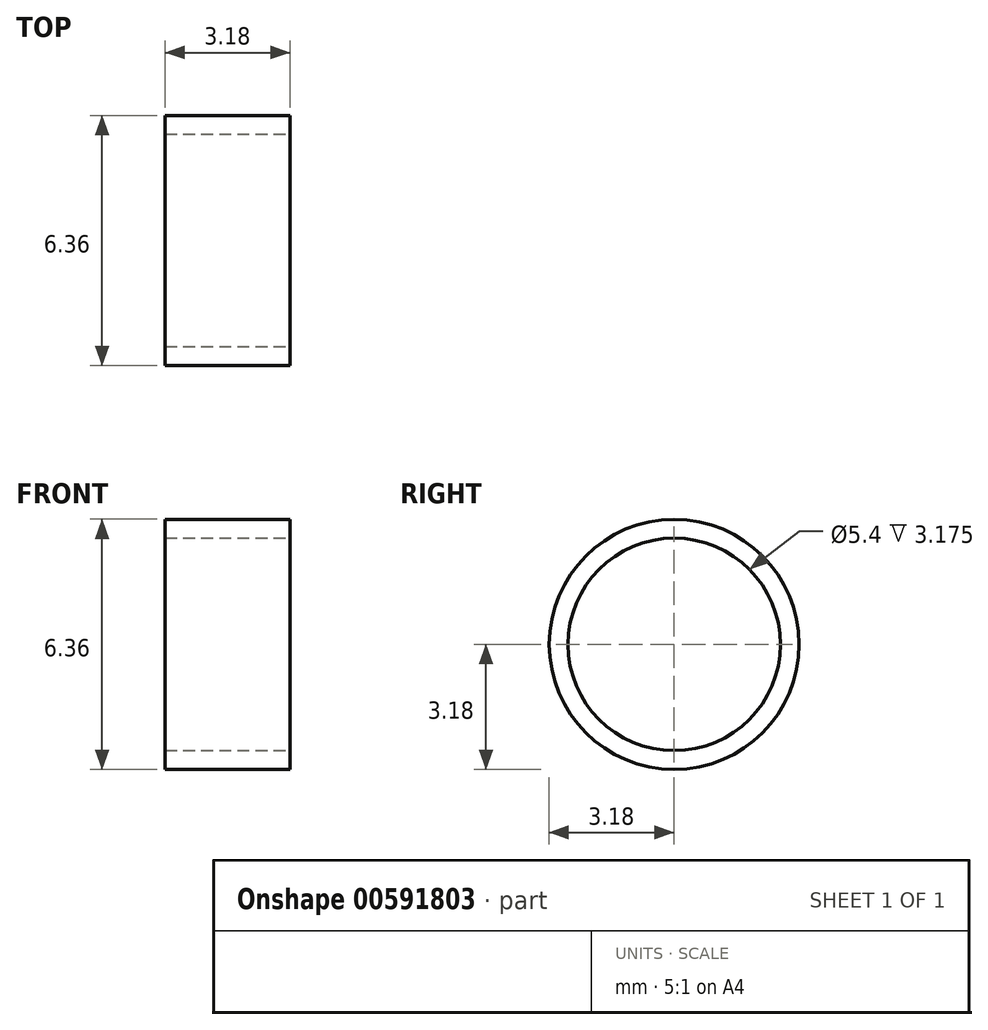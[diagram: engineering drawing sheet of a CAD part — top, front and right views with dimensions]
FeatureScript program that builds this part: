
annotation { "Feature Type Name" : "Feature", "Feature Type Description" : "" }
export const myFeature = defineFeature(function(context is Context, id is Id, definition is map)
    precondition{}
    {
        {
            var Q0;
            Q0=qCreatedBy(makeId("Right.planeOp"),FACE);
            var sketch = newSketch(context, id + "F0", { "sketchPlane" : qUnion([Q0])});
            skCircle(sketch, "E0", {"center": v(0, 0) * mm, "radius": 12.7 * mm});
            skSolve(sketch);
        }
        {
            var Q0;
            Q0=makeQuery(id+"F0.imprint","IMPRINT",FACE,{"disambiguationData":[TD([[makeQuery(id+"F0.imprint","IMPRINT",EDGE,{"derivedFrom":sQuery(id+"F0.wireOp",EDGE,"E0")}),1.0]])]});
            extrude(context, id + "F1", {"entities" : qUnion([Q0]), "depth" : 12.7 * mm, "offsetDistance" : 25.4 * mm});
        }
        {
            var Q0;
            Q0=makeQuery(id+"F1.opExtrude","CAP_FACE",FACE,{"disambiguationData":[OSD([sQuery(id+"F0.wireOp",EDGE,"E0")])],"isStart":false});
            var sketch = newSketch(context, id + "F2", { "sketchPlane" : qUnion([Q0])});
            skCircle(sketch, "E1", {"center": v(0, 0) * mm, "radius": 9.53 * mm});
            skSolve(sketch);
        }
        {
            var Q0;
            Q0=sQuery(id+"F2.wireOp",VERTEX,"E1.center");
            var Q1;
            Q1=makeQuery(id+"F1.opExtrude","SWEPT_BODY",BODY,{"disambiguationData":[OSD([sQuery(id+"F0.wireOp",EDGE,"E0")])]});
            hole(context, id + "F3", {"style" : HoleStyle.SIMPLE, "endStyle" : HoleEndStyle.THROUGH, "holeDiameter" : 21.59 * mm, "majorDiameter" : 6.35 * mm, "isTappedThrough" : true, "tappedDepth" : 12.7 * mm, "tapClearance" : 3, "locations" : qUnion([Q0]), "scope" : qUnion([Q1])});
        }
        {
            var Q0;
            Q0=makeQuery(id+"F1.opExtrude","SWEPT_BODY",BODY,{"disambiguationData":[OSD([sQuery(id+"F0.wireOp",EDGE,"E0")])]});
            var Q1;
            Q1=qCreatedBy(makeId("Origin.pointOp"),VERTEX);
            transform(context, id + "F4", {"entities" : qUnion([Q0]), "transformType" : TransformType.SCALE_UNIFORMLY, "scale" : .25, "scalePoint" : qUnion([Q1]), "makeCopy" : false});
        }
    });
